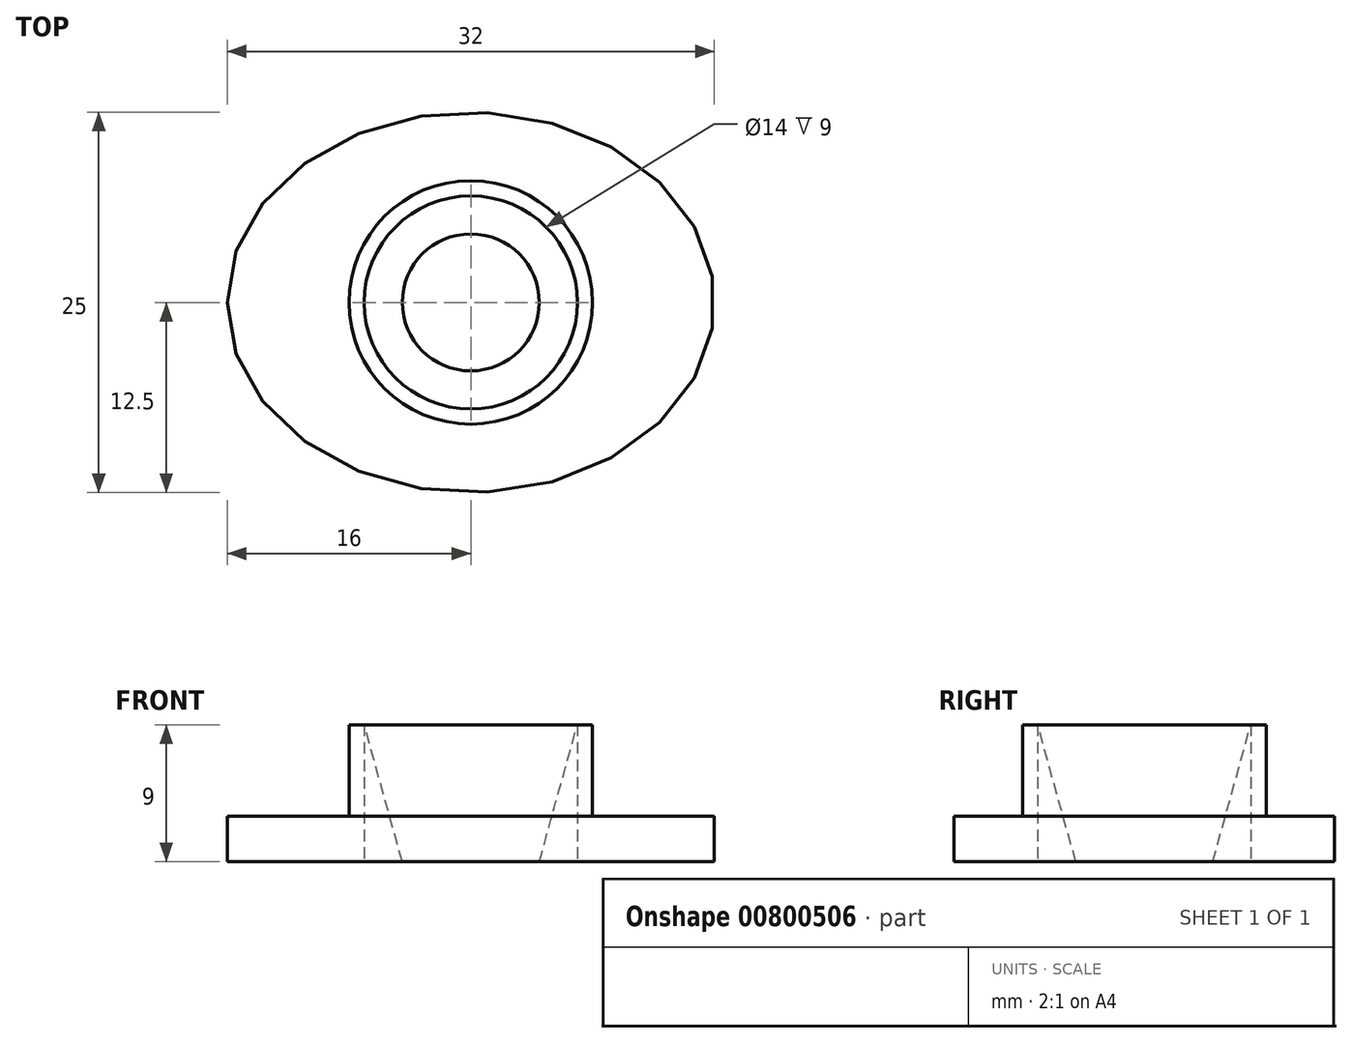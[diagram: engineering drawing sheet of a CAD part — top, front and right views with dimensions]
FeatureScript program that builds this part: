
annotation { "Feature Type Name" : "Feature", "Feature Type Description" : "" }
export const myFeature = defineFeature(function(context is Context, id is Id, definition is map)
    precondition{}
    {
        {
            var Q0;
            Q0=qCreatedBy(makeId("Top.planeOp"),FACE);
            var sketch = newSketch(context, id + "F0", { "sketchPlane" : qUnion([Q0])});
            skEllipse(sketch, "E0", {"center": v(0, 0) * mm, "majorRadius": 16 * mm, "minorRadius": 12.5 * mm, "majorAxis": v(-1, 0)});
            skCircle(sketch, "E1", {"center": v(0, 0) * mm, "radius": 4.5 * mm});
            skCircle(sketch, "E2", {"center": v(0, 0) * mm, "radius": 8 * mm});
            skCircle(sketch, "E3", {"center": v(0, 0) * mm, "radius": 7 * mm});
            skSolve(sketch);
        }
        {
            var Q0;
            Q0=makeQuery(id+"F0.imprint","IMPRINT",FACE,{"disambiguationData":[TD([[makeQuery(id+"F0.imprint","IMPRINT",EDGE,{"derivedFrom":sQuery(id+"F0.wireOp",EDGE,"E0")}),1.0]])]});
            extrude(context, id + "F1", {"entities" : qUnion([Q0]), "depth" : 3 * mm, "offsetDistance" : 25 * mm});
        }
        {
            var Q0;
            Q0=makeQuery(id+"F0.imprint","IMPRINT",FACE,{"disambiguationData":[TD([[makeQuery(id+"F0.imprint","IMPRINT",EDGE,{"derivedFrom":sQuery(id+"F0.wireOp",EDGE,"E2")}),1.0]])]});
            extrude(context, id + "F2", {"entities" : qUnion([Q0]), "operationType" : NewBodyOperationType.ADD, "depth" : 9 * mm, "offsetDistance" : 25 * mm});
        }
        {
            var Q0;
            Q0=makeQuery(id+"F0.imprint","IMPRINT",FACE,{"disambiguationData":[TD([[makeQuery(id+"F0.imprint","IMPRINT",EDGE,{"derivedFrom":sQuery(id+"F0.wireOp",EDGE,"E1")}),-1.0]])]});
            var Q1;
            Q1=makeQuery(id+"F2.opExtrude","CAP_FACE",FACE,{"disambiguationData":[OSD([sQuery(id+"F0.wireOp",EDGE,"E2"),sQuery(id+"F0.wireOp",EDGE,"E3")])],"isStart":false});
            extrude(context, id + "F3", {"entities" : qUnion([Q0]), "endBound" : BoundingType.UP_TO_SURFACE, "depth" : 25 * mm, "endBoundEntityFace" : qUnion([Q1]), "offsetDistance" : 25 * mm});
        }
        {
            var Q0;
            Q0=makeQuery(id+"F0.imprint","IMPRINT",FACE,{"disambiguationData":[TD([[makeQuery(id+"F0.imprint","IMPRINT",EDGE,{"derivedFrom":sQuery(id+"F0.wireOp",EDGE,"E1")}),1.0]])]});
            extrude(context, id + "F4", {"entities" : qUnion([Q0]), "operationType" : NewBodyOperationType.REMOVE, "oppositeDirection" : true, "depth" : 25 * mm, "offsetDistance" : 25 * mm});
        }
        {
            var Q0;
            Q0=makeQuery(id+"F3.opExtrude","CAP_EDGE",EDGE,{"disambiguationData":[OSD([sQuery(id+"F0.wireOp",EDGE,"E1")])],"isStart":false});
            chamfer(context, id + "F5", {"entities" : qUnion([Q0]), "chamferType" : ChamferType.TWO_OFFSETS, "width1" : 9 * mm, "oppositeDirection" : false, "width2" : 2.5 * mm, "tangentPropagation" : true});
        }
    });
